# Revit family: ЛД_Eng
name_source: partatom
category: Оборудование
units: mm (PartAtom-declared; Revit-internal decimal feet)

## family parameters
Всегда вертикально = Да
Классификация = Нет
На основе рабочей плоскости = Нет
Общий = Нет
При загрузке вырезать с полостями = Нет
Размер круглого соединителя = Использовать диаметр
Тип детали = Нормальный
Точка принадлежности помещению = Нет

## types (5) — shared parameters
00_20_Manufacturer = Vents
00_20_Name = Axial fan
Casing Material = Plastic, opaque, white
Frequency = 50 Гц
Load Classification = HVAC
Maintenance zone material = <По категории>
Number of Fase = 1
URL = https://ventilation-system.com
Voltage = 230 В
Изготовитель = Vents
zero-valued in all types: Отметка по умолчанию

## per-type parameters (varying)
| type | Amperage | Apparent Load | B | D | Diameter | Dn | Height | L | L1 | L2 | L22 | Length | Maximum Air Flow | Power | Sound pressure level at 3 m distance | Weight | Width |
| 100 LD | 0.085 А | 20 Вт | 152 мм | 100 мм | 100 мм | 104 мм | 152 мм | 126 мм | 30 мм | 96 мм | 64 мм | 126 мм | 88.0 м³/ч | 14 Вт | 33 dBA | 0.60 кг | 152 мм |
| 125 LD | 0.100 А | 23 Вт | 177 мм | 125 мм | 125 мм | 129 мм | 177 мм | 135 мм | 34 мм | 101 мм | 67 мм | 135 мм | 167.0 м³/ч | 16 Вт | 34 dBA | 0.74 кг | 177 мм |
| 150 LD | 0.130 А | 30 Вт | 206 мм | 150 мм | 150 мм | 154 мм | 206 мм | 154 мм | 36 мм | 118 мм | 79 мм | 154 мм | 265.0 м³/ч | 24 Вт | 37 dBA | 0.96 кг | 206 мм |
| 100 LD Turbo | 0.100 А | 23 Вт | 152 мм | 100 мм | 100 мм | 104 мм | 152 мм | 126 мм | 30 мм | 96 мм | 64 мм | 126 мм | 115.0 м³/ч | 16 Вт | 36 dBA | 0.68 кг | 152 мм |
| 125 LD Turbo | 0.105 А | 24 Вт | 177 мм | 125 мм | 125 мм | 129 мм | 177 мм | 135 мм | 34 мм | 101 мм | 67 мм | 135 мм | 209.0 м³/ч | 24 Вт | 36 dBA | 0.84 кг | 177 мм |

note: column(s) folded — value = type name in every type: 00_20_Type
